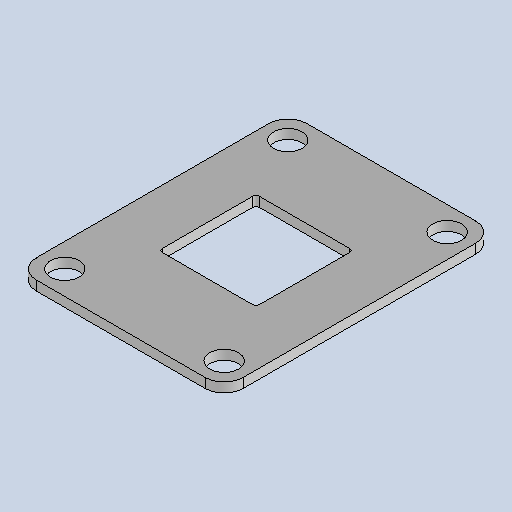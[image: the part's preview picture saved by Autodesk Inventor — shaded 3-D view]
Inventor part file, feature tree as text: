
AUTODESK INVENTOR PART (.ipt)
format: ipt  version: 2025.1 (Build 291241020, 241B)  size: 186,880 bytes
history: native  units: mm
features: other x3, chamfer x2, sketch x2, sheet_metal_op x1
ambient origin geometry x8: Origin, YZ Plane, XZ Plane, XY Plane, X Axis, Y Axis, Z Axis, Center Point
bodies: Body1 (feature_tree)
feature tree (8):
  sheet_metal_op  "Face3"
  chamfer  "Corner Round1"
  chamfer  "Corner Round2"
  sketch  "Sketch1"  dims[d154=65.0mm]
  other  "Plate5"
  sketch  "Sketch9"  dims[d155=85.0mm d156=3.0mm d172=30.5mm d173=70.0mm d174=9.0mm d175=50.0mm d176=3.0mm d177=0.0mm d178=6.0mm d179=1.0mm]
  other  "Cut2"
  other  "Definition1"
